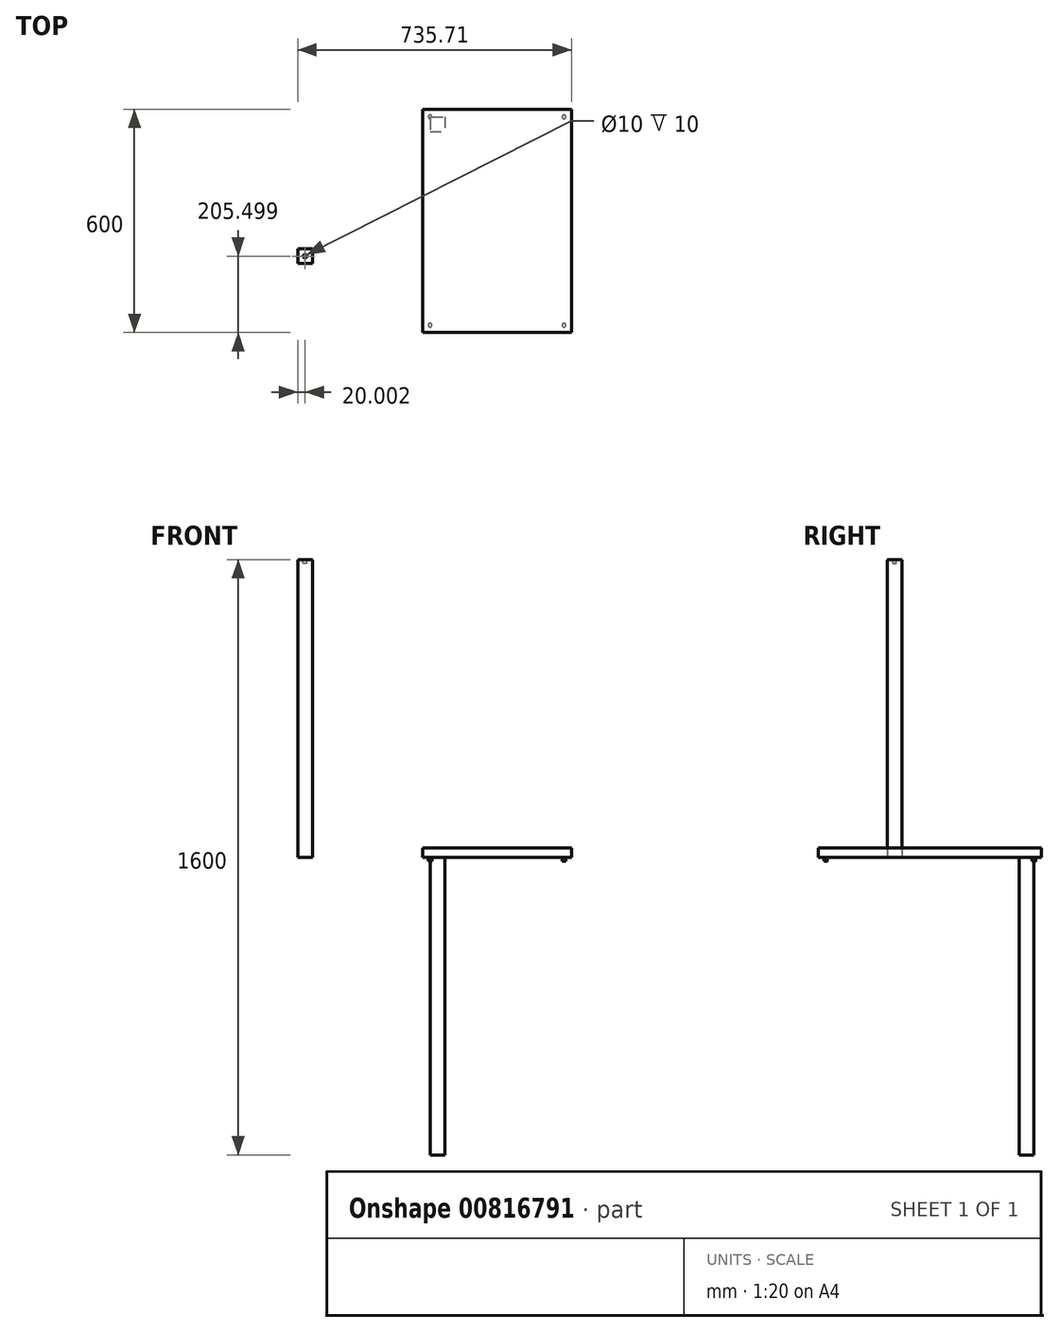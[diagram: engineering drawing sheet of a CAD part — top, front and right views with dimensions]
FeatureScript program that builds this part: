
annotation { "Feature Type Name" : "Feature", "Feature Type Description" : "" }
export const myFeature = defineFeature(function(context is Context, id is Id, definition is map)
    precondition{}
    {
        {
            var Q0;
            Q0=qCreatedBy(makeId("Top.planeOp"),FACE);
            var sketch = newSketch(context, id + "F0", { "sketchPlane" : qUnion([Q0])});
            skLineSegment(sketch, "E0.bottom", {"start": v(-32.43, 31.96) * mm, "end": v(7.57, 31.96) * mm});
            skLineSegment(sketch, "E0.top", {"start": v(-32.43, -8.04) * mm, "end": v(7.57, -8.04) * mm});
            skLineSegment(sketch, "E0.left", {"start": v(-32.43, 31.96) * mm, "end": v(-32.43, -8.04) * mm});
            skLineSegment(sketch, "E0.right", {"start": v(7.57, 31.96) * mm, "end": v(7.57, -8.04) * mm});
            skSolve(sketch);
        }
        {
            var Q0;
            Q0=makeQuery(id+"F0.imprint","IMPRINT",FACE,{"disambiguationData":[TD([[makeQuery(id+"F0.imprint","IMPRINT",EDGE,{"derivedFrom":sQuery(id+"F0.wireOp",EDGE,"E0.bottom")}),-1.0]])]});
            extrude(context, id + "F1", {"entities" : qUnion([Q0]), "depth" : 800 * mm, "offsetDistance" : 25 * mm});
        }
        {
            var Q0;
            Q0=qCreatedBy(makeId("Top.planeOp"),FACE);
            var sketch = newSketch(context, id + "F2", { "sketchPlane" : qUnion([Q0])});
            skLineSegment(sketch, "E1.bottom", {"start": v(303.28, 406.46) * mm, "end": v(703.28, 406.46) * mm});
            skLineSegment(sketch, "E1.top", {"start": v(303.28, -193.54) * mm, "end": v(703.28, -193.54) * mm});
            skLineSegment(sketch, "E1.left", {"start": v(303.28, 406.46) * mm, "end": v(303.28, -193.54) * mm});
            skLineSegment(sketch, "E1.right", {"start": v(703.28, 406.46) * mm, "end": v(703.28, -193.54) * mm});
            skSolve(sketch);
        }
        {
            var Q0;
            Q0=makeQuery(id+"F2.imprint","IMPRINT",FACE,{"disambiguationData":[TD([[makeQuery(id+"F2.imprint","IMPRINT",EDGE,{"derivedFrom":sQuery(id+"F2.wireOp",EDGE,"E1.bottom")}),-1.0]])]});
            extrude(context, id + "F3", {"entities" : qUnion([Q0]), "depth" : 25 * mm, "offsetDistance" : 25 * mm});
        }
        {
            var Q0;
            Q0=makeQuery(id+"F3.opExtrude","CAP_FACE",FACE,{"disambiguationData":[OSD([sQuery(id+"F2.wireOp",EDGE,"E1.bottom"),sQuery(id+"F2.wireOp",EDGE,"E1.top"),sQuery(id+"F2.wireOp",EDGE,"E1.left"),sQuery(id+"F2.wireOp",EDGE,"E1.right")])],"isStart":false});
            var sketch = newSketch(context, id + "F4", { "sketchPlane" : qUnion([Q0])});
            skLineSegment(sketch, "E2", {"start": v(503.28, 406.46) * mm, "end": v(503.28, -193.54) * mm});
            skCircle(sketch, "E3", {"center": v(323.28, -173.54) * mm, "radius": 5 * mm});
            skLineSegment(sketch, "E4", {"start": v(303.28, 106.46) * mm, "end": v(703.28, 106.46) * mm});
            skCircle(sketch, "E5.MirrorC", {"center": v(683.28, -173.54) * mm, "radius": 5 * mm});
            skCircle(sketch, "E6.MirrorC", {"center": v(323.28, 386.46) * mm, "radius": 5 * mm});
            skCircle(sketch, "E7.MirrorC", {"center": v(683.28, 386.46) * mm, "radius": 5 * mm});
            skSolve(sketch);
        }
        {
            var Q0;
            Q0 = qSketchRegion(id + "F4", true);
            extrude(context, id + "F5", {"entities" : qUnion([Q0]), "operationType" : NewBodyOperationType.ADD, "oppositeDirection" : true, "depth" : 35 * mm, "offsetDistance" : 25 * mm});
        }
        {
            var Q0;
            Q0=makeQuery(id+"F1.opExtrude","CAP_FACE",FACE,{"disambiguationData":[OSD([sQuery(id+"F0.wireOp",EDGE,"E0.bottom"),sQuery(id+"F0.wireOp",EDGE,"E0.top"),sQuery(id+"F0.wireOp",EDGE,"E0.left"),sQuery(id+"F0.wireOp",EDGE,"E0.right")])],"isStart":false});
            var sketch = newSketch(context, id + "F6", { "sketchPlane" : qUnion([Q0])});
            skCircle(sketch, "E8", {"center": v(-12.43, 11.96) * mm, "radius": 5 * mm});
            skPoint(sketch, "E8.centerSnap0", {"position": v(-12.43, -8.04) * mm});
            skPoint(sketch, "E8.centerSnap1", {"position": v(-32.43, 11.96) * mm});
            skSolve(sketch);
        }
        {
            var Q0;
            Q0 = qSketchRegion(id + "F6", true);
            extrude(context, id + "F7", {"entities" : qUnion([Q0]), "operationType" : NewBodyOperationType.REMOVE, "oppositeDirection" : true, "depth" : 10 * mm, "offsetDistance" : 25 * mm});
        }
        {
            var Q0;
            Q0=makeQuery(id+"F3.opExtrude","CAP_FACE",FACE,{"disambiguationData":[OSD([sQuery(id+"F2.wireOp",EDGE,"E1.bottom"),sQuery(id+"F2.wireOp",EDGE,"E1.top"),sQuery(id+"F2.wireOp",EDGE,"E1.left"),sQuery(id+"F2.wireOp",EDGE,"E1.right")])],"isStart":true});
            var sketch = newSketch(context, id + "F8", { "sketchPlane" : qUnion([Q0])});
            skLineSegment(sketch, "E9.bottom", {"start": v(323.28, -386.46) * mm, "end": v(363.28, -386.46) * mm});
            skLineSegment(sketch, "E9.top", {"start": v(323.28, -346.46) * mm, "end": v(363.28, -346.46) * mm});
            skLineSegment(sketch, "E9.left", {"start": v(323.28, -386.46) * mm, "end": v(323.28, -346.46) * mm});
            skLineSegment(sketch, "E9.right", {"start": v(363.28, -386.46) * mm, "end": v(363.28, -346.46) * mm});
            skSolve(sketch);
        }
        {
            var Q0;
            Q0 = qSketchRegion(id + "F8", true);
            extrude(context, id + "F9", {"entities" : qUnion([Q0]), "operationType" : NewBodyOperationType.ADD, "depth" : 800 * mm, "offsetDistance" : 25 * mm});
        }
    });
